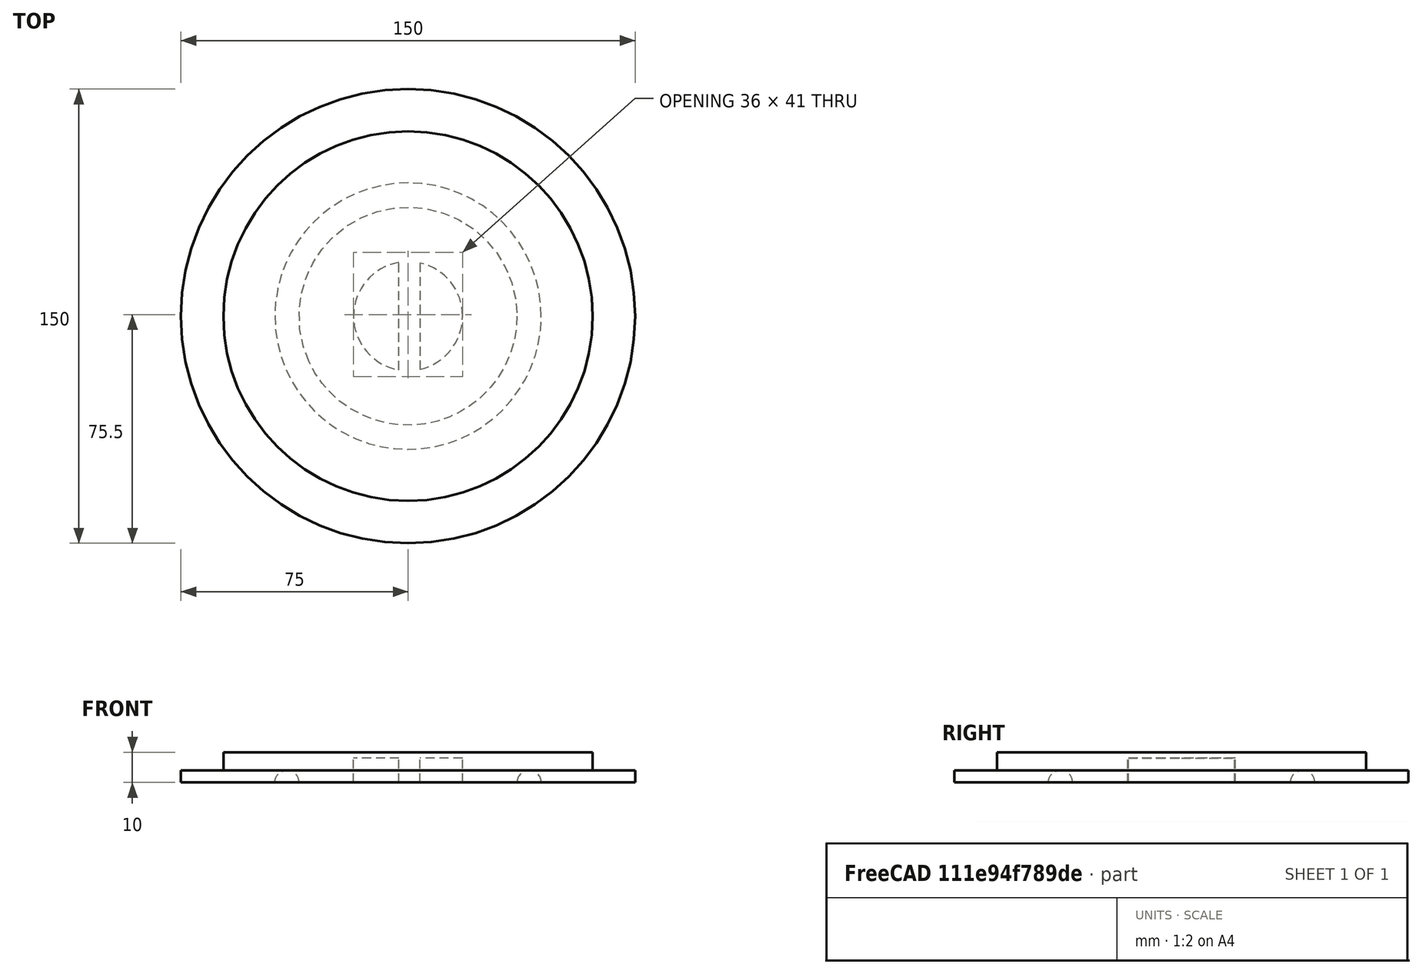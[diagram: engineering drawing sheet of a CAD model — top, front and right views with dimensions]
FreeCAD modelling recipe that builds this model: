
FCSTD DOCUMENT
Label: rat.social.interaction.cover
objects: Part::Cylinder×4, Part::MultiFuse×3, Part::Cut×2, Part::Box×1, Part::Torus×1
note: 11 computed .brp shape members not serialized (recipe doc carries the construction recipe); baked Part::Feature solids carry a one-line shape summary decoded from their .brp

FEATURE [Part::Cylinder] Cylinder
  Angle = 360
  Height = 10
  Radius = 61
FEATURE [Part::Cylinder] Cylinder001
  Angle = 360
  Height = 4
  Radius = 75
FEATURE [Part::Cylinder] Cylinder002
  Angle = 360
  Height = 10
  Radius = 18
FEATURE [Part::Box] Box
  Height = 10
  Length = 7
  Placement = pos=(-3,-20,0) rot=(0,0,1;0rad)
  Width = 41
FEATURE [Part::MultiFuse] Fusion
  Shapes = -> [Cylinder,Cylinder001]
FEATURE [Part::Cut] Cut
  Base = -> Fusion
  Tool = -> Cylinder002
FEATURE [Part::MultiFuse] Fusion001
  Shapes = -> [Cut,Box]
FEATURE [Part::Cylinder] Cylinder003
  Angle = 360
  Height = 2
  Placement = pos=(0,0,8) rot=(0,0,1;0rad)
  Radius = 18
FEATURE [Part::MultiFuse] Fusion002
  Shapes = -> [Fusion001,Cylinder003]
FEATURE [Part::Torus] Torus
  Angle1 = -180
  Angle2 = 180
  Angle3 = 360
  Radius1 = 40
  Radius2 = 4
FEATURE [Part::Cut] Cut001
  Base = -> Fusion002
  Tool = -> Torus
